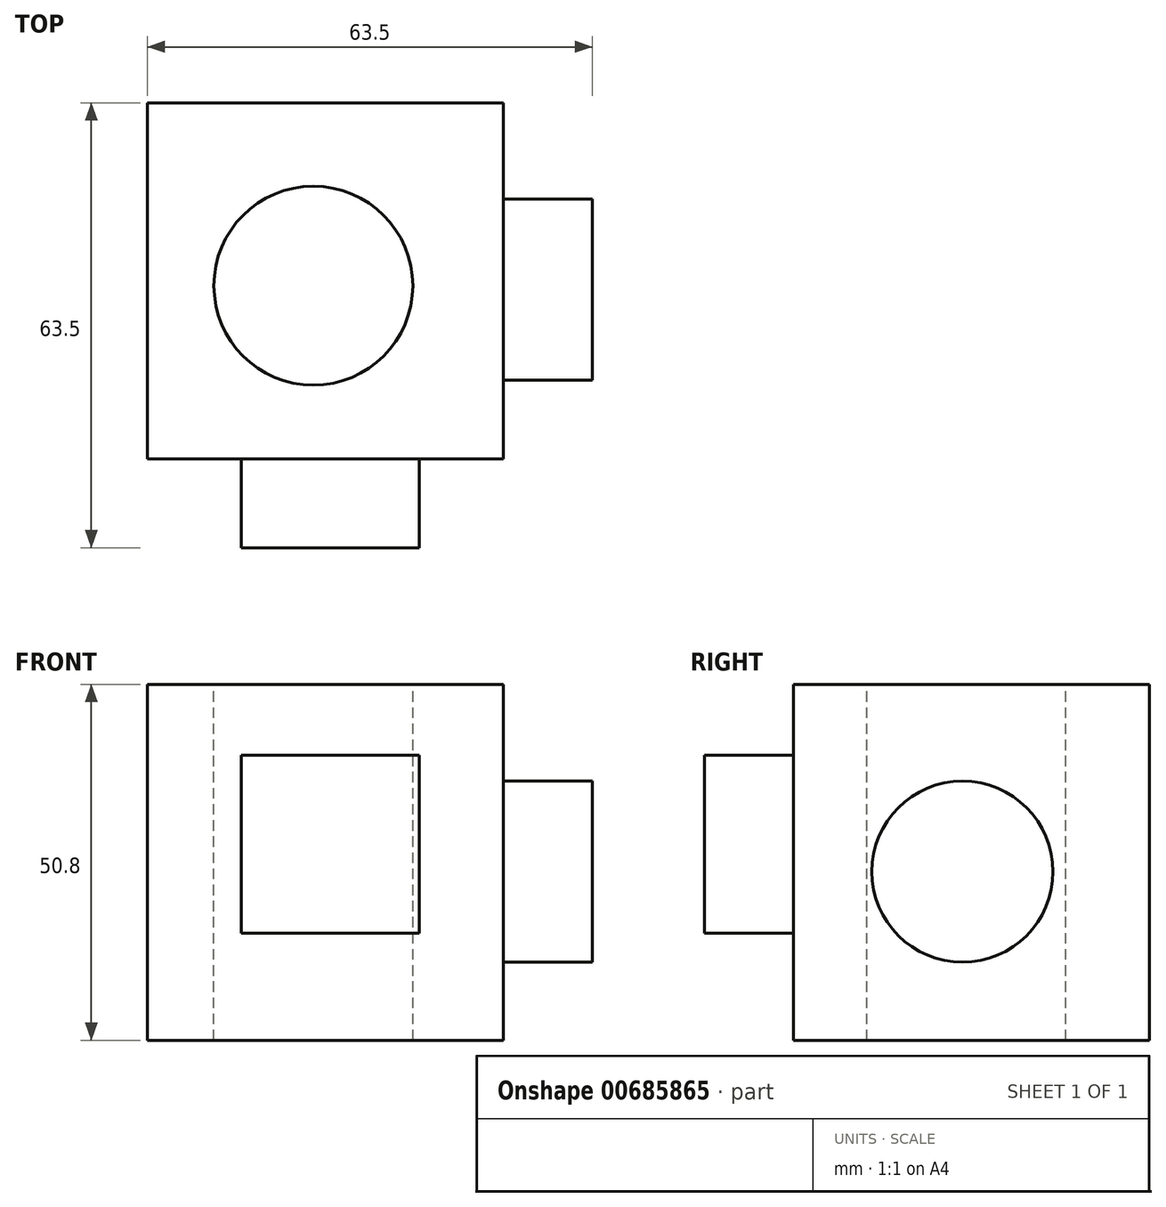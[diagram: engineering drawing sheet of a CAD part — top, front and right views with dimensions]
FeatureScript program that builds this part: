
annotation { "Feature Type Name" : "Feature", "Feature Type Description" : "" }
export const myFeature = defineFeature(function(context is Context, id is Id, definition is map)
    precondition{}
    {
        {
            var Q0;
            Q0=qCreatedBy(makeId("Front.planeOp"),FACE);
            var sketch = newSketch(context, id + "F0", { "sketchPlane" : qUnion([Q0])});
            skLineSegment(sketch, "E0.bottom", {"start": v(-16.14, 22.06) * mm, "end": v(34.66, 22.06) * mm});
            skLineSegment(sketch, "E0.top", {"start": v(-16.14, -28.74) * mm, "end": v(34.66, -28.74) * mm});
            skLineSegment(sketch, "E0.left", {"start": v(-16.14, 22.06) * mm, "end": v(-16.14, -28.74) * mm});
            skLineSegment(sketch, "E0.right", {"start": v(34.66, 22.06) * mm, "end": v(34.66, -28.74) * mm});
            skSolve(sketch);
        }
        {
            var Q0;
            Q0 = qSketchRegion(id + "F0", true);
            extrude(context, id + "F1", {"entities" : qUnion([Q0]), "depth" : 50.8 * mm, "offsetDistance" : 25.4 * mm});
        }
        {
            var Q0;
            Q0=makeQuery(id+"F1.opExtrude","CAP_FACE",FACE,{"disambiguationData":[OSD([sQuery(id+"F0.wireOp",EDGE,"E0.bottom"),sQuery(id+"F0.wireOp",EDGE,"E0.top"),sQuery(id+"F0.wireOp",EDGE,"E0.left"),sQuery(id+"F0.wireOp",EDGE,"E0.right")])],"isStart":false});
            var sketch = newSketch(context, id + "F2", { "sketchPlane" : qUnion([Q0])});
            skLineSegment(sketch, "E1.bottom", {"start": v(-2.77, 11.94) * mm, "end": v(22.63, 11.94) * mm});
            skLineSegment(sketch, "E1.top", {"start": v(-2.77, -13.46) * mm, "end": v(22.63, -13.46) * mm});
            skLineSegment(sketch, "E1.left", {"start": v(-2.77, 11.94) * mm, "end": v(-2.77, -13.46) * mm});
            skLineSegment(sketch, "E1.right", {"start": v(22.63, 11.94) * mm, "end": v(22.63, -13.46) * mm});
            skSolve(sketch);
        }
        {
            var Q0;
            Q0 = qSketchRegion(id + "F2", true);
            extrude(context, id + "F3", {"entities" : qUnion([Q0]), "operationType" : NewBodyOperationType.ADD, "depth" : 12.7 * mm, "offsetDistance" : 25.4 * mm});
        }
        {
            var Q0;
            Q0=makeQuery(id+"F1.opExtrude","SWEPT_FACE",FACE,{"disambiguationData":[OSD([sQuery(id+"F0.wireOp",EDGE,"E0.right")])]});
            var sketch = newSketch(context, id + "F4", { "sketchPlane" : qUnion([Q0])});
            skCircle(sketch, "E2", {"center": v(-26.68, -4.68) * mm, "radius": 12.92 * mm});
            skSolve(sketch);
        }
        {
            var Q0;
            Q0 = qSketchRegion(id + "F4", true);
            extrude(context, id + "F5", {"entities" : qUnion([Q0]), "operationType" : NewBodyOperationType.ADD, "depth" : 12.7 * mm, "offsetDistance" : 25.4 * mm});
        }
        {
            var Q0;
            Q0=makeQuery(id+"F1.opExtrude","SWEPT_FACE",FACE,{"disambiguationData":[OSD([sQuery(id+"F0.wireOp",EDGE,"E0.bottom")])]});
            var sketch = newSketch(context, id + "F6", { "sketchPlane" : qUnion([Q0])});
            skCircle(sketch, "E3", {"center": v(7.54, -26.1) * mm, "radius": 14.2 * mm});
            skSolve(sketch);
        }
        {
            var Q0;
            Q0 = qSketchRegion(id + "F6", true);
            extrude(context, id + "F7", {"entities" : qUnion([Q0]), "operationType" : NewBodyOperationType.REMOVE, "oppositeDirection" : true, "depth" : 50.8 * mm, "offsetDistance" : 25.4 * mm});
        }
    });
